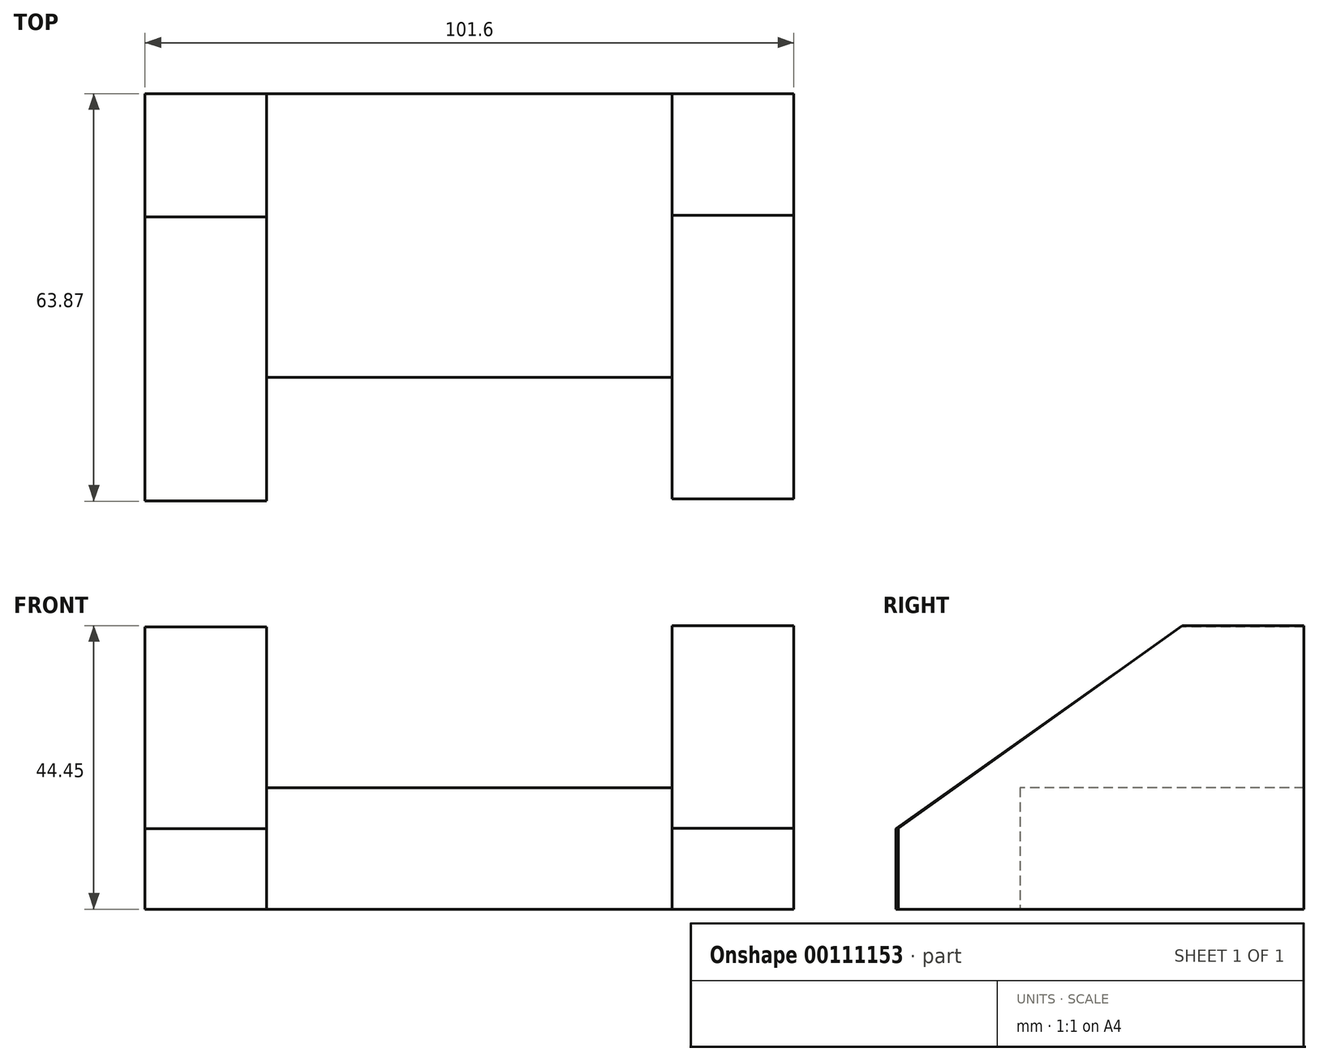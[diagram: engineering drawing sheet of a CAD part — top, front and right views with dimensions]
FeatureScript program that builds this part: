
annotation { "Feature Type Name" : "Feature", "Feature Type Description" : "" }
export const myFeature = defineFeature(function(context is Context, id is Id, definition is map)
    precondition{}
    {
        {
            var Q0;
            Q0=qCreatedBy(makeId("Right.planeOp"),FACE);
            var sketch = newSketch(context, id + "F0", { "sketchPlane" : qUnion([Q0])});
            skLineSegment(sketch, "E0", {"start": v(0, 0) * mm, "end": v(0, 44.45) * mm});
            skLineSegment(sketch, "E1", {"start": v(0, 0) * mm, "end": v(-63.5, 0) * mm});
            skLineSegment(sketch, "E2", {"start": v(-63.5, 0) * mm, "end": v(-63.5, 12.7) * mm});
            skLineSegment(sketch, "E3", {"start": v(0, 44.45) * mm, "end": v(-19.05, 44.45) * mm});
            skLineSegment(sketch, "E4", {"start": v(-19.05, 44.45) * mm, "end": v(-63.5, 12.7) * mm});
            skSolve(sketch);
        }
        {
            var Q0;
            Q0 = qSketchRegion(id + "F0", true);
            extrude(context, id + "F1", {"entities" : qUnion([Q0]), "depth" : 19.05 * mm});
        }
        {
            var Q0;
            Q0=makeQuery(id+"F1.opExtrude","CAP_FACE",FACE,{"disambiguationData":[OSD([sQuery(id+"F0.wireOp",EDGE,"E0"),sQuery(id+"F0.wireOp",EDGE,"E1"),sQuery(id+"F0.wireOp",EDGE,"E2"),sQuery(id+"F0.wireOp",EDGE,"E3"),sQuery(id+"F0.wireOp",EDGE,"E4")])],"isStart":true});
            var sketch = newSketch(context, id + "F2", { "sketchPlane" : qUnion([Q0])});
            skLineSegment(sketch, "E5", {"start": v(0, 0) * mm, "end": v(0, 19.05) * mm});
            skLineSegment(sketch, "E6", {"start": v(0, 19.05) * mm, "end": v(44.45, 19.05) * mm});
            skLineSegment(sketch, "E7", {"start": v(44.45, 19.05) * mm, "end": v(44.45, 0) * mm});
            skLineSegment(sketch, "E8", {"start": v(44.45, 0) * mm, "end": v(0, 0) * mm});
            skSolve(sketch);
        }
        {
            var Q0;
            Q0=makeQuery(id+"F2.imprint","IMPRINT",FACE,{"disambiguationData":[TD([[makeQuery(id+"F2.imprint","IMPRINT",EDGE,{"derivedFrom":sQuery(id+"F2.wireOp",EDGE,"E5")}),-1.0]])]});
            extrude(context, id + "F3", {"entities" : qUnion([Q0]), "operationType" : NewBodyOperationType.ADD, "depth" : 63.5 * mm});
        }
        {
            var Q0;
            Q0=makeQuery(id+"F3.opExtrude","CAP_FACE",FACE,{"disambiguationData":[OSD([sQuery(id+"F2.wireOp",EDGE,"E5"),sQuery(id+"F2.wireOp",EDGE,"E6"),sQuery(id+"F2.wireOp",EDGE,"E7"),sQuery(id+"F2.wireOp",EDGE,"E8")])],"isStart":false});
            var sketch = newSketch(context, id + "F4", { "sketchPlane" : qUnion([Q0])});
            skLineSegment(sketch, "E9", {"start": v(0, 0) * mm, "end": v(0, 44.21) * mm});
            skLineSegment(sketch, "E10", {"start": v(0, 44.21) * mm, "end": v(19.3, 44.21) * mm});
            skLineSegment(sketch, "E11", {"start": v(19.3, 44.21) * mm, "end": v(63.87, 12.63) * mm});
            skLineSegment(sketch, "E12", {"start": v(63.87, 12.63) * mm, "end": v(63.87, 0) * mm});
            skLineSegment(sketch, "E13", {"start": v(0, 0) * mm, "end": v(63.87, 0) * mm});
            skLineSegment(sketch, "E14", {"start": v(22.23, 19.05) * mm, "end": v(0, 0) * mm});
            skSolve(sketch);
        }
        {
            var Q0;
            Q0 = qSketchRegion(id + "F4", true);
            extrude(context, id + "F5", {"entities" : qUnion([Q0]), "operationType" : NewBodyOperationType.ADD, "depth" : 19.05 * mm});
        }
    });
